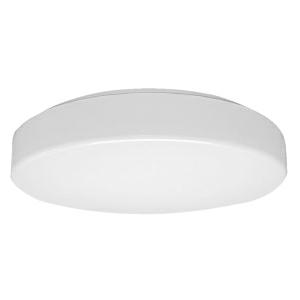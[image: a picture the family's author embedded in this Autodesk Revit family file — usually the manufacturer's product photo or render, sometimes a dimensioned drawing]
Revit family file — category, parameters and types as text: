
# Revit family: oblo_fit_-_oba_2000_840_00813349_81ba
name_source: partatom
category: Lighting Fixtures
units: mm (PartAtom-declared; Revit-internal decimal feet)

## family parameters
Cut with Voids When Loaded = No
Host = Face
Light Source = No
Part Type = Normal
Room Calculation Point = No
Round Connector Dimension = Use Diameter
Shared = No

## types (1)
- OBLO.fit - OBA 2000/840 (1 x LED, 2100 lm, 4000K)
    Apparent Load = 22 VA
    Approval mark = CE
    CIE Flux Codes = 41 72 91 84 100
    Color Rendering = 80-89
    Color Temperature = 4000K
    Control Gear = Electronic ballast
    Default Elevation = 1800 mm
    Description = OBA 2000/840|Surface-mounted luminaire.|light source:   Cold white   |work equipment: Power supply unit|luminous flux: 2100 lm|light distribution: Direct|class of protection: I|technology: Switchable|mains lead: Direct power supply|glare control: without|
    Frequency = 50 Hz, 60 Hz
    Height = 85 mm
    Lamp = 1 x LED
    Lamp Light Flux = 2100 lm
    Lamp count = 1
    Length = 370 mm
    Luminous efficacy = 95 lm/W
    Manufacturer = Waldmann
    ModVariant = No
    Model = 00813349
    Mounting Place = Ceiling
    Mounting Type = Surface mounted
    Number of Poles = 1
    OnlyDefault = Yes
    Power Factor = 1
    Product Name = OBLO.fit - OBA 2000/840
    Product group = Ceiling mounted luminaire
    ProductGroupID = 3
    Protection Class = Protection class I
    Protection Degree = IP 40
    RLX_Detail_Level = 1
    RLX_Emergency_Light_Flux = 0 lm
    RLX_Emergency_Type = 0
    RLX_Emergency_Type_DB = No
    RlxData = <blob elided: 22245 chars, md5=fa1d6d4f>
    Socket = socket
    Standby Power = 0 W
    System Light Flux = 2100 lm
    System Power = 22 W
    Type Comments = Product without accessories
    Type Image = oblo_led.jpg
    URL = http://relux.com
    VarID = ---
    Voltage = 230 V
    Voltage Range = 220-240 V
    Weight = 0.00 kg
    Width = 0 mm  [stored 0 ft]

note: [stored X ft] marks values corroborated as IEEE doubles in the binary element streams (Revit-internal decimal feet)

## geometry (parser evidence)
native form markers: Blend x4, Sweep x12
no freeform markers — native parametric forms only
